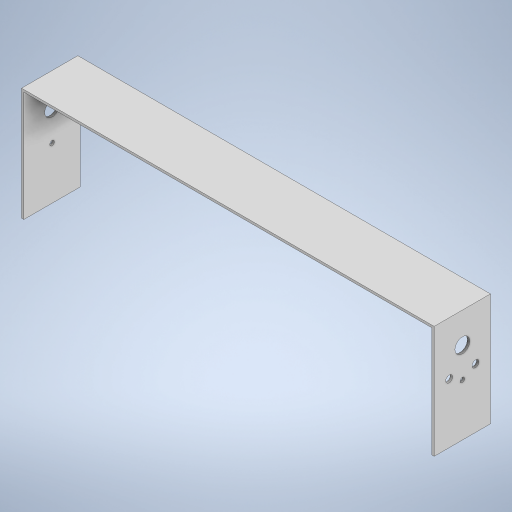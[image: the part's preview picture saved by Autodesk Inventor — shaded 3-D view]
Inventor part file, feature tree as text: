
AUTODESK INVENTOR PART (.ipt)
format: ipt  version: 2024 (Build 280153000, 153)  size: 252,928 bytes
history: native  units: in
note: dims shown in document units (in); Inventor stores cm internally (conversion verified against a paired STEP export)
features: extrude x4, sketch x4
ambient origin geometry x8: Origin, YZ Plane, XZ Plane, XY Plane, X Axis, Y Axis, Z Axis, Center Point
bodies: Solid1 (feature_tree)
feature tree (8):
  extrude  "Extrusion1"  Depth=3.0in
  extrude  "Extrusion2"  Depth=0.0625in
  extrude  "Extrusion3"  Depth=0.0625in
  extrude  "Extrusion4"  Depth=1.5in
  sketch  "Sketch1"  dims[d0=11.0in d1=3.0in]
  sketch  "Sketch2"  dims[d2=1.5in d3=0.0in d4=0.0625in]
  sketch  "Sketch3"  dims[d5=0.0625in d6=0.0625in]
  sketch  "Sketch4"  dims[d7=1.5in d8=0.0in d9=0.3976in d10=0.75in d11=0.0in d12=0.0in d13=0.125in d15=0.8in d16=0.4in d17=0.6in d18=0.1875in d19=1.0in d20=0.0in]
